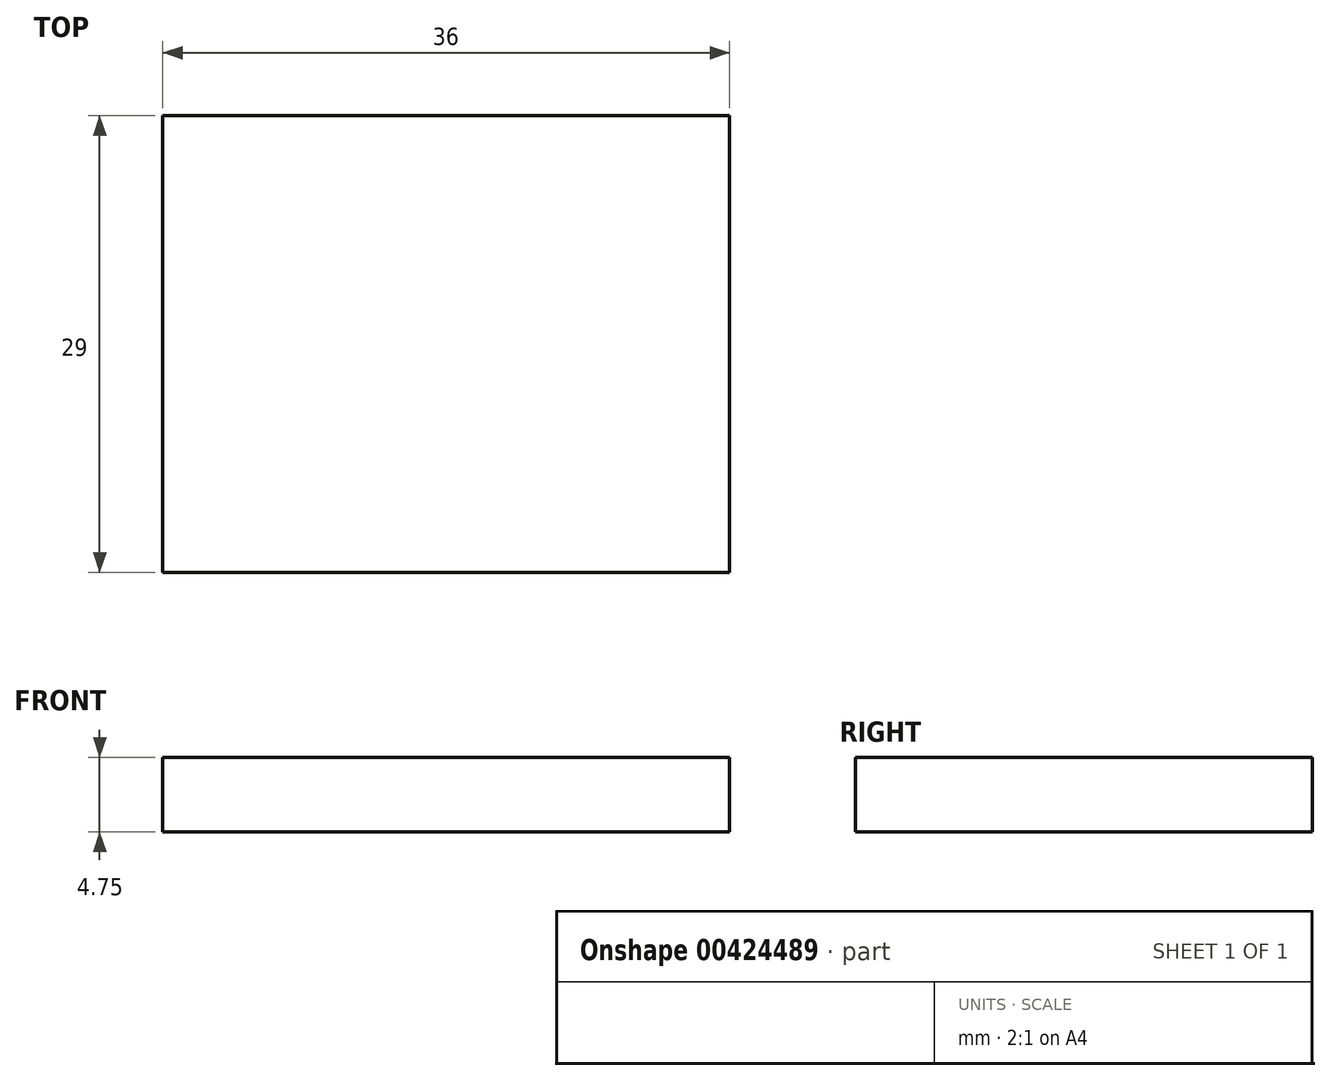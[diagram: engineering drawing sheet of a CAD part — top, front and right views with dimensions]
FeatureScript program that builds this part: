
annotation { "Feature Type Name" : "Feature", "Feature Type Description" : "" }
export const myFeature = defineFeature(function(context is Context, id is Id, definition is map)
    precondition{}
    {
        {
            var Q0;
            Q0=qCreatedBy(makeId("Top.planeOp"),FACE);
            var sketch = newSketch(context, id + "F0", { "sketchPlane" : qUnion([Q0])});
            skLineSegment(sketch, "E0.bottom", {"start": v(18, 14.5) * mm, "end": v(-18, 14.5) * mm});
            skLineSegment(sketch, "E0.top", {"start": v(18, -14.5) * mm, "end": v(-18, -14.5) * mm});
            skLineSegment(sketch, "E0.left", {"start": v(18, 14.5) * mm, "end": v(18, -14.5) * mm});
            skLineSegment(sketch, "E0.right", {"start": v(-18, 14.5) * mm, "end": v(-18, -14.5) * mm});
            skPoint(sketch, "E0.middle", {"position": v(0, 0) * mm});
            skSolve(sketch);
        }
        {
            var Q0;
            Q0=makeQuery(id+"F0.imprint","IMPRINT",FACE,{"disambiguationData":[TD([[makeQuery(id+"F0.imprint","IMPRINT",EDGE,{"derivedFrom":sQuery(id+"F0.wireOp",EDGE,"E0.bottom")}),1.0]])]});
            extrude(context, id + "F1", {"entities" : qUnion([Q0]), "depth" : 4.75 * mm});
        }
    });
